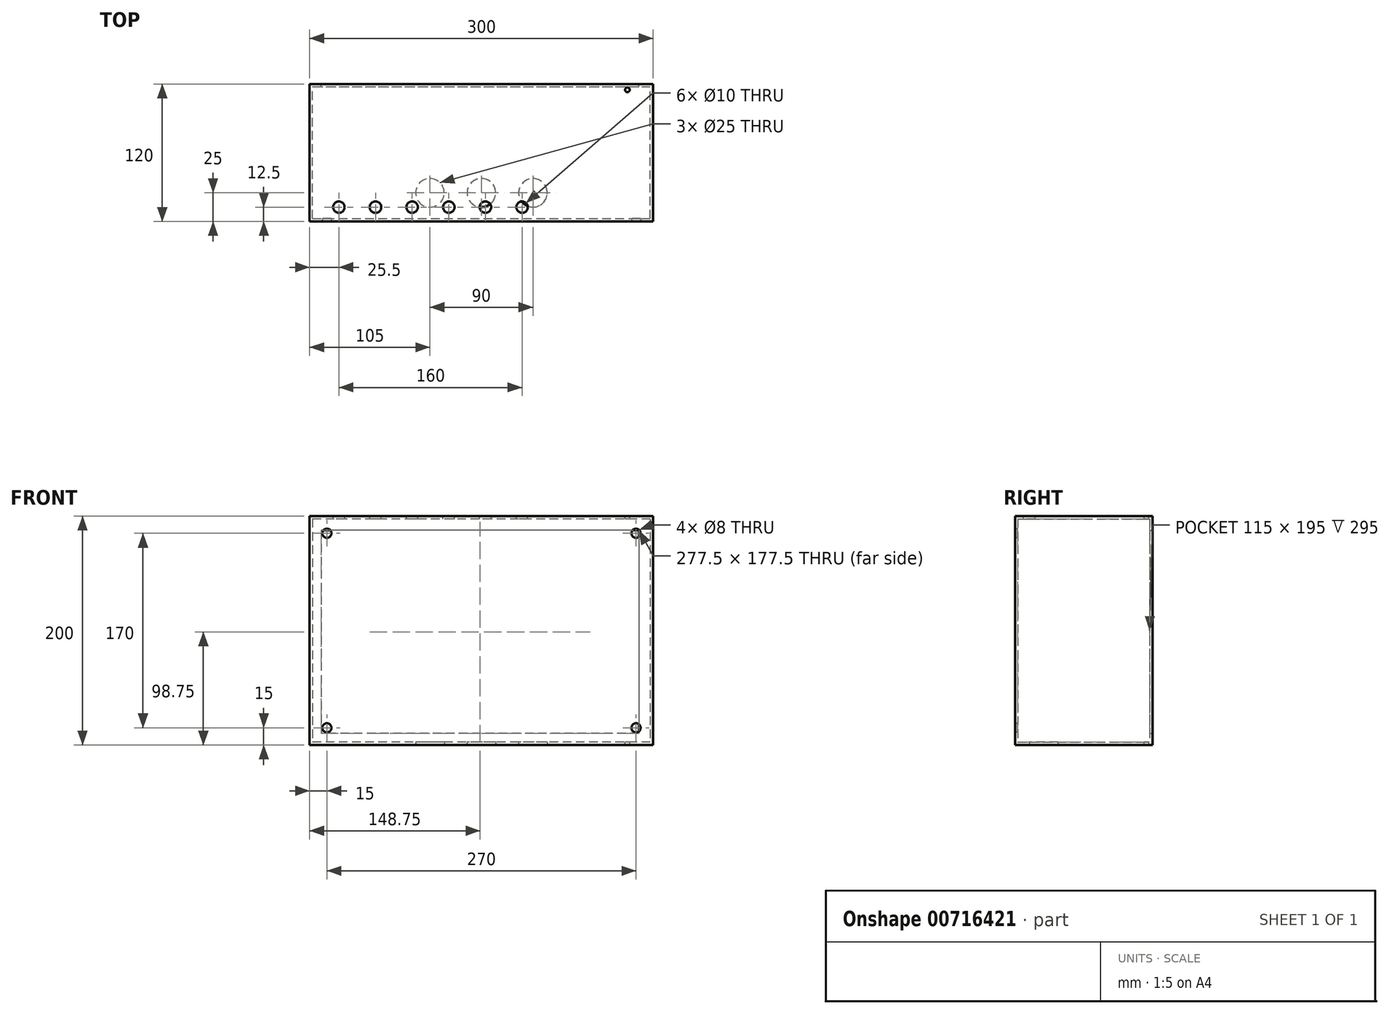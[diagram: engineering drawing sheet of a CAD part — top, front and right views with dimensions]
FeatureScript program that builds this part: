
annotation { "Feature Type Name" : "Feature", "Feature Type Description" : "" }
export const myFeature = defineFeature(function(context is Context, id is Id, definition is map)
    precondition{}
    {
        {
            var Q0;
            Q0=qCreatedBy(makeId("Top.planeOp"),FACE);
            var sketch = newSketch(context, id + "F0", { "sketchPlane" : qUnion([Q0])});
            skLineSegment(sketch, "E0.bottom", {"start": v(0, 0) * mm, "end": v(300, 0) * mm});
            skLineSegment(sketch, "E0.top", {"start": v(0, 120) * mm, "end": v(300, 120) * mm});
            skLineSegment(sketch, "E0.left", {"start": v(0, 0) * mm, "end": v(0, 120) * mm});
            skLineSegment(sketch, "E0.right", {"start": v(300, 0) * mm, "end": v(300, 120) * mm});
            skSolve(sketch);
        }
        {
            var Q0;
            Q0=qSketchRegion(id+"F0",true);
            extrude(context, id + "F1", {"entities" : qUnion([Q0]), "depth" : 200 * mm, "offsetDistance" : 25 * mm});
        }
        {
            var Q0;
            Q0=makeQuery(id+"F1.opExtrude","SWEPT_FACE",FACE,{"disambiguationData":[OSD([sQuery(id+"F0.wireOp",EDGE,"E0.top")])]});
            shell(context, id + "F2", {"entities" : qUnion([Q0]), "thickness" : 2.5 * mm});
        }
        {
            var Q0;
            Q0=makeQuery(id+"F1.opExtrude","SWEPT_FACE",FACE,{"disambiguationData":[OSD([sQuery(id+"F0.wireOp",EDGE,"E0.top")])]});
            var sketch = newSketch(context, id + "F3", { "sketchPlane" : qUnion([Q0])});
            skLineSegment(sketch, "E1.bottom", {"start": v(-297.5, 197.5) * mm, "end": v(0, 197.5) * mm});
            skLineSegment(sketch, "E1.top", {"start": v(-297.5, 0) * mm, "end": v(0, 0) * mm});
            skLineSegment(sketch, "E1.left", {"start": v(-297.5, 197.5) * mm, "end": v(-297.5, 0) * mm});
            skLineSegment(sketch, "E1.right", {"start": v(0, 197.5) * mm, "end": v(0, 0) * mm});
            skLineSegment(sketch, "E2.0", {"start": v(-10, 187.5) * mm, "end": v(-10, 10) * mm});
            skLineSegment(sketch, "E2.1", {"start": v(-287.5, 187.5) * mm, "end": v(-10, 187.5) * mm});
            skLineSegment(sketch, "E2.2", {"start": v(-287.5, 187.5) * mm, "end": v(-287.5, 10) * mm});
            skLineSegment(sketch, "E2.3", {"start": v(-287.5, 10) * mm, "end": v(-10, 10) * mm});
            skSolve(sketch);
        }
        {
            var Q0;
            Q0=qSketchRegion(id+"F3",true);
            extrude(context, id + "F4", {"entities" : qUnion([Q0]), "operationType" : NewBodyOperationType.ADD, "oppositeDirection" : true, "depth" : 2.5 * mm, "offsetDistance" : 25 * mm});
        }
        {
            var Q0;
            Q0=makeQuery(id+"F1.opExtrude","CAP_FACE",FACE,{"disambiguationData":[OSD([sQuery(id+"F0.wireOp",EDGE,"E0.bottom"),sQuery(id+"F0.wireOp",EDGE,"E0.top"),sQuery(id+"F0.wireOp",EDGE,"E0.left"),sQuery(id+"F0.wireOp",EDGE,"E0.right")])],"isStart":false});
            var sketch = newSketch(context, id + "F5", { "sketchPlane" : qUnion([Q0])});
            skCircle(sketch, "E3", {"center": v(277.5, 115) * mm, "radius": 2 * mm});
            skSolve(sketch);
        }
        {
            var Q0;
            Q0=qSketchRegion(id+"F5",true);
            extrude(context, id + "F6", {"entities" : qUnion([Q0]), "operationType" : NewBodyOperationType.REMOVE, "endBound" : BoundingType.THROUGH_ALL, "oppositeDirection" : true, "depth" : 25 * mm, "offsetDistance" : 25 * mm});
        }
        {
            var Q0;
            Q0=makeQuery(id+"F5.imprint","IMPRINT",FACE,{"disambiguationData":[TD([[makeQuery(id+"F5.imprint","IMPRINT",EDGE,{"derivedFrom":sQuery(id+"F5.wireOp",EDGE,"E3")}),-1.0]])]});
            var sketch = newSketch(context, id + "F7", { "sketchPlane" : qUnion([Q0])});
            skCircle(sketch, "E4", {"center": v(185.5, 12.5) * mm, "radius": 5 * mm});
            skCircle(sketch, "E5.1.0.0", {"center": v(153.5, 12.5) * mm, "radius": 5 * mm});
            skCircle(sketch, "E5.2.0.0", {"center": v(121.5, 12.5) * mm, "radius": 5 * mm});
            skCircle(sketch, "E5.3.0.0", {"center": v(89.5, 12.5) * mm, "radius": 5 * mm});
            skCircle(sketch, "E5.4.0.0", {"center": v(57.5, 12.5) * mm, "radius": 5 * mm});
            skCircle(sketch, "E5.5.0.0", {"center": v(25.5, 12.5) * mm, "radius": 5 * mm});
            skLineSegment(sketch, "E5.direction1", {"start": v(185.5, 12.5) * mm, "end": v(153.5, 12.5) * mm, "construction": true});
            skSolve(sketch);
        }
        {
            var Q0;
            Q0 = qSketchRegion(id + "F7", true);
            extrude(context, id + "F8", {"entities" : qUnion([Q0]), "operationType" : NewBodyOperationType.REMOVE, "oppositeDirection" : true, "depth" : 5 * mm, "offsetDistance" : 25 * mm});
        }
        {
            var Q0;
            Q0=makeQuery(id+"F1.opExtrude","SWEPT_FACE",FACE,{"disambiguationData":[OSD([sQuery(id+"F0.wireOp",EDGE,"E0.bottom")])]});
            var sketch = newSketch(context, id + "F9", { "sketchPlane" : qUnion([Q0])});
            skCircle(sketch, "E6", {"center": v(285, 185) * mm, "radius": 4 * mm});
            skLineSegment(sketch, "E7", {"start": v(300, 100) * mm, "end": v(0, 100) * mm, "construction": true});
            skLineSegment(sketch, "E8", {"start": v(150, 0) * mm, "end": v(150, 200) * mm, "construction": true});
            skCircle(sketch, "E9.MirrorC", {"center": v(285, 15) * mm, "radius": 4 * mm});
            skCircle(sketch, "E10.MirrorC", {"center": v(15, 185) * mm, "radius": 4 * mm});
            skCircle(sketch, "E11.MirrorC", {"center": v(15, 15) * mm, "radius": 4 * mm});
            skSolve(sketch);
        }
        {
            var Q0;
            Q0 = qSketchRegion(id + "F9", true);
            extrude(context, id + "F10", {"entities" : qUnion([Q0]), "operationType" : NewBodyOperationType.REMOVE, "oppositeDirection" : true, "depth" : 2.5 * mm, "offsetDistance" : 25 * mm});
        }
        {
            var Q0;
            Q0=makeQuery(id+"F0.imprint","IMPRINT",FACE,{"disambiguationData":[TD([[makeQuery(id+"F0.imprint","IMPRINT",EDGE,{"derivedFrom":sQuery(id+"F0.wireOp",EDGE,"E0.bottom")}),1.0]])]});
            var sketch = newSketch(context, id + "F11", { "sketchPlane" : qUnion([Q0])});
            skLineSegment(sketch, "E12", {"start": v(300.58, 25) * mm, "end": v(0, 25) * mm, "construction": true});
            skLineSegment(sketch, "E13", {"start": v(150, 130.26) * mm, "end": v(150, -17.05) * mm, "construction": true});
            skCircle(sketch, "E14", {"center": v(150, 25) * mm, "radius": 12.5 * mm});
            skCircle(sketch, "E15", {"center": v(195, 25) * mm, "radius": 12.5 * mm});
            skCircle(sketch, "E16", {"center": v(105, 25) * mm, "radius": 12.5 * mm});
            skSolve(sketch);
        }
        {
            var Q0;
            Q0 = qSketchRegion(id + "F11", true);
            extrude(context, id + "F12", {"entities" : qUnion([Q0]), "operationType" : NewBodyOperationType.REMOVE, "depth" : 3 * mm, "offsetDistance" : 25 * mm});
        }
    });
